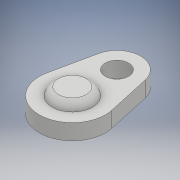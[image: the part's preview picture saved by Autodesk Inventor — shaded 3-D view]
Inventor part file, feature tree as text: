
AUTODESK INVENTOR PART (.ipt)
format: ipt  version: 2017 (Build 210142000, 142)  size: 136,192 bytes
history: native  units: mm
features: extrude x3, sketch x3, fillet x1
ambient origin geometry x8: Origin, YZ Plane, XZ Plane, XY Plane, X Axis, Y Axis, Z Axis, Center Point
bodies: Solid1 (feature_tree)
feature tree (7):
  extrude  "Extrusion1"  Depth=2.5mm
  extrude  "Extrusion2"  Depth=2.5mm
  fillet  "Fillet1"  Radius=1.5mm
  extrude  "Extrusion3"  Depth=1.0mm
  sketch  "Sketch1"  dims[d0=2.5mm d1=6.0mm]
  sketch  "Sketch2"  dims[d2=2.0mm d3=0.0mm d4=2.5mm d5=6.0mm d6=1.5mm d7=0.0mm]
  sketch  "Sketch3"  dims[d8=2.5mm d9=1.0mm d10=10.0mm d11=0.0mm]
